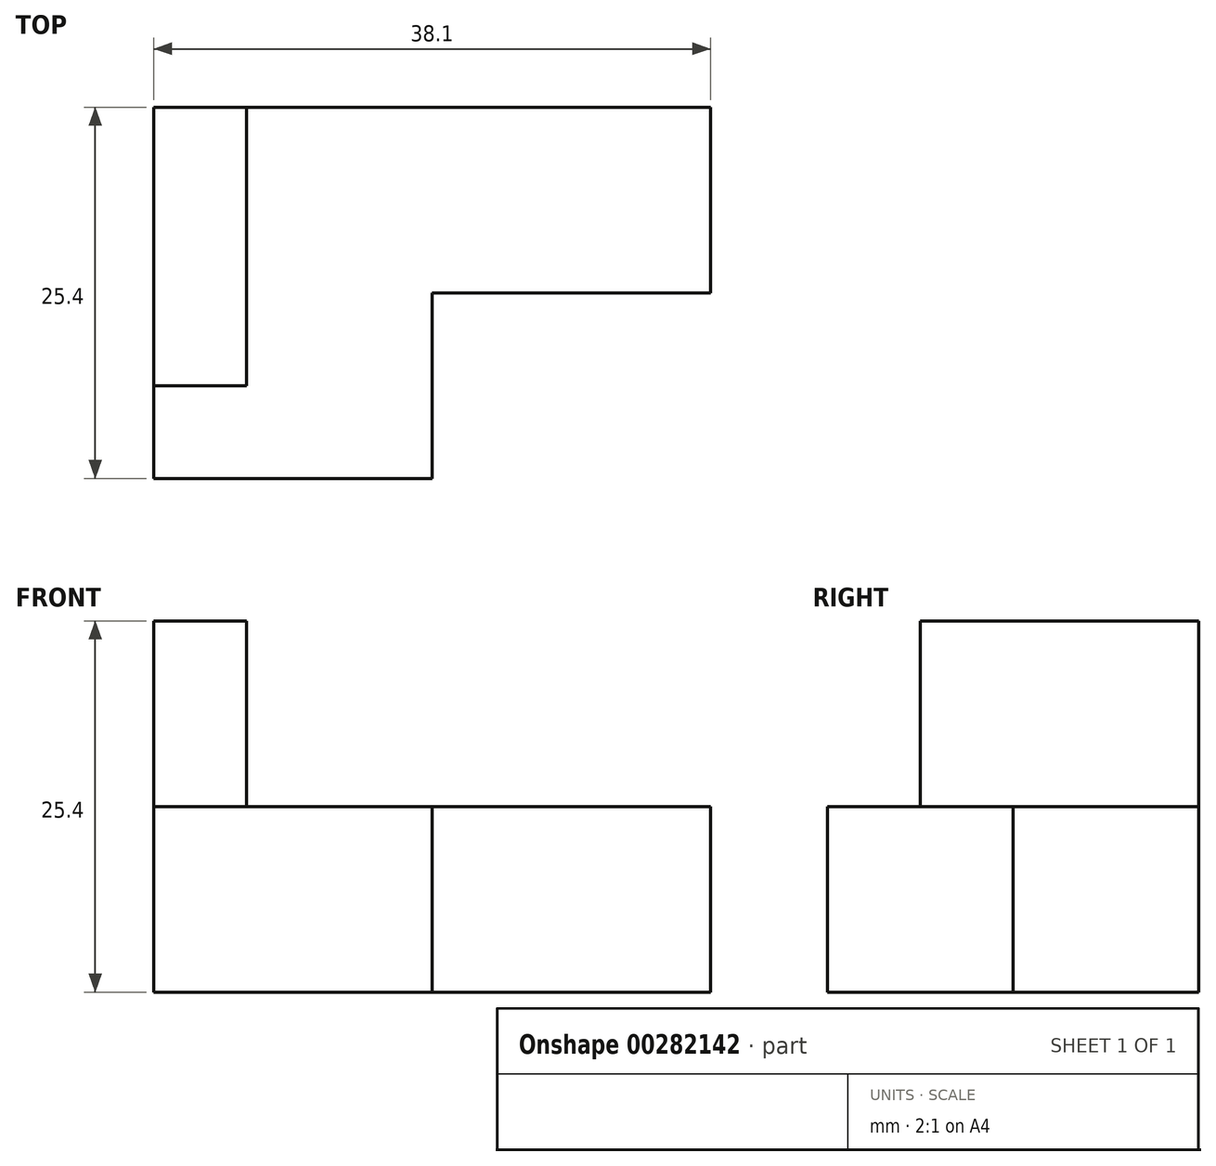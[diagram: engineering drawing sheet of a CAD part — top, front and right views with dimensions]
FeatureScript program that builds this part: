
annotation { "Feature Type Name" : "Feature", "Feature Type Description" : "" }
export const myFeature = defineFeature(function(context is Context, id is Id, definition is map)
    precondition{}
    {
        {
            var Q0;
            Q0=qCreatedBy(makeId("Top.planeOp"),FACE);
            var sketch = newSketch(context, id + "F0", { "sketchPlane" : qUnion([Q0])});
            skLineSegment(sketch, "E0", {"start": v(0, 25.4) * mm, "end": v(38.1, 25.4) * mm});
            skLineSegment(sketch, "E1", {"start": v(38.1, 25.4) * mm, "end": v(38.1, 12.7) * mm});
            skLineSegment(sketch, "E2", {"start": v(38.1, 12.7) * mm, "end": v(19.05, 12.7) * mm});
            skLineSegment(sketch, "E3", {"start": v(19.05, 12.7) * mm, "end": v(19.05, 0) * mm});
            skLineSegment(sketch, "E4", {"start": v(19.05, 0) * mm, "end": v(0, 0) * mm});
            skLineSegment(sketch, "E5", {"start": v(0, 0) * mm, "end": v(0, 25.4) * mm});
            skSolve(sketch);
        }
        {
            var Q0;
            Q0=makeQuery(id+"F0.imprint","IMPRINT",FACE,{"disambiguationData":[TD([[makeQuery(id+"F0.imprint","IMPRINT",EDGE,{"derivedFrom":sQuery(id+"F0.wireOp",EDGE,"PsjwM1Fs-Ib9d-Rhgv-Sft3-6QIyTsX0ZUIn.bottom")}),-1.0]])]});
            var Q1;
            Q1=makeQuery(id+"F0.imprint","IMPRINT",FACE,{"disambiguationData":[TD([[makeQuery(id+"F0.imprint","IMPRINT",EDGE,{"derivedFrom":sQuery(id+"F0.wireOp",EDGE,"E0")}),-1.0]])]});
            extrude(context, id + "F1", {"entities" : qUnion([Q0, Q1]), "depth" : 12.7 * mm});
        }
        {
            var Q0;
            Q0=makeQuery(id+"F1.opExtrude","CAP_FACE",FACE,{"disambiguationData":[OSD([sQuery(id+"F0.wireOp",EDGE,"E0"),sQuery(id+"F0.wireOp",EDGE,"E1"),sQuery(id+"F0.wireOp",EDGE,"E2"),sQuery(id+"F0.wireOp",EDGE,"E3"),sQuery(id+"F0.wireOp",EDGE,"E4"),sQuery(id+"F0.wireOp",EDGE,"E5")])],"isStart":false});
            var sketch = newSketch(context, id + "F2", { "sketchPlane" : qUnion([Q0])});
            skLineSegment(sketch, "E6.bottom", {"start": v(0, 25.4) * mm, "end": v(6.35, 25.4) * mm});
            skLineSegment(sketch, "E6.top", {"start": v(0, 6.35) * mm, "end": v(6.35, 6.35) * mm});
            skLineSegment(sketch, "E6.left", {"start": v(0, 25.4) * mm, "end": v(0, 6.35) * mm});
            skLineSegment(sketch, "E6.right", {"start": v(6.35, 25.4) * mm, "end": v(6.35, 6.35) * mm});
            skSolve(sketch);
        }
        {
            var Q0;
            Q0=makeQuery(id+"F2.imprint","IMPRINT",FACE,{"disambiguationData":[TD([[makeQuery(id+"F2.imprint","IMPRINT",EDGE,{"derivedFrom":sQuery(id+"F2.wireOp",EDGE,"E6.bottom")}),-1.0]])]});
            extrude(context, id + "F3", {"entities" : qUnion([Q0]), "operationType" : NewBodyOperationType.ADD, "depth" : 12.7 * mm});
        }
    });
